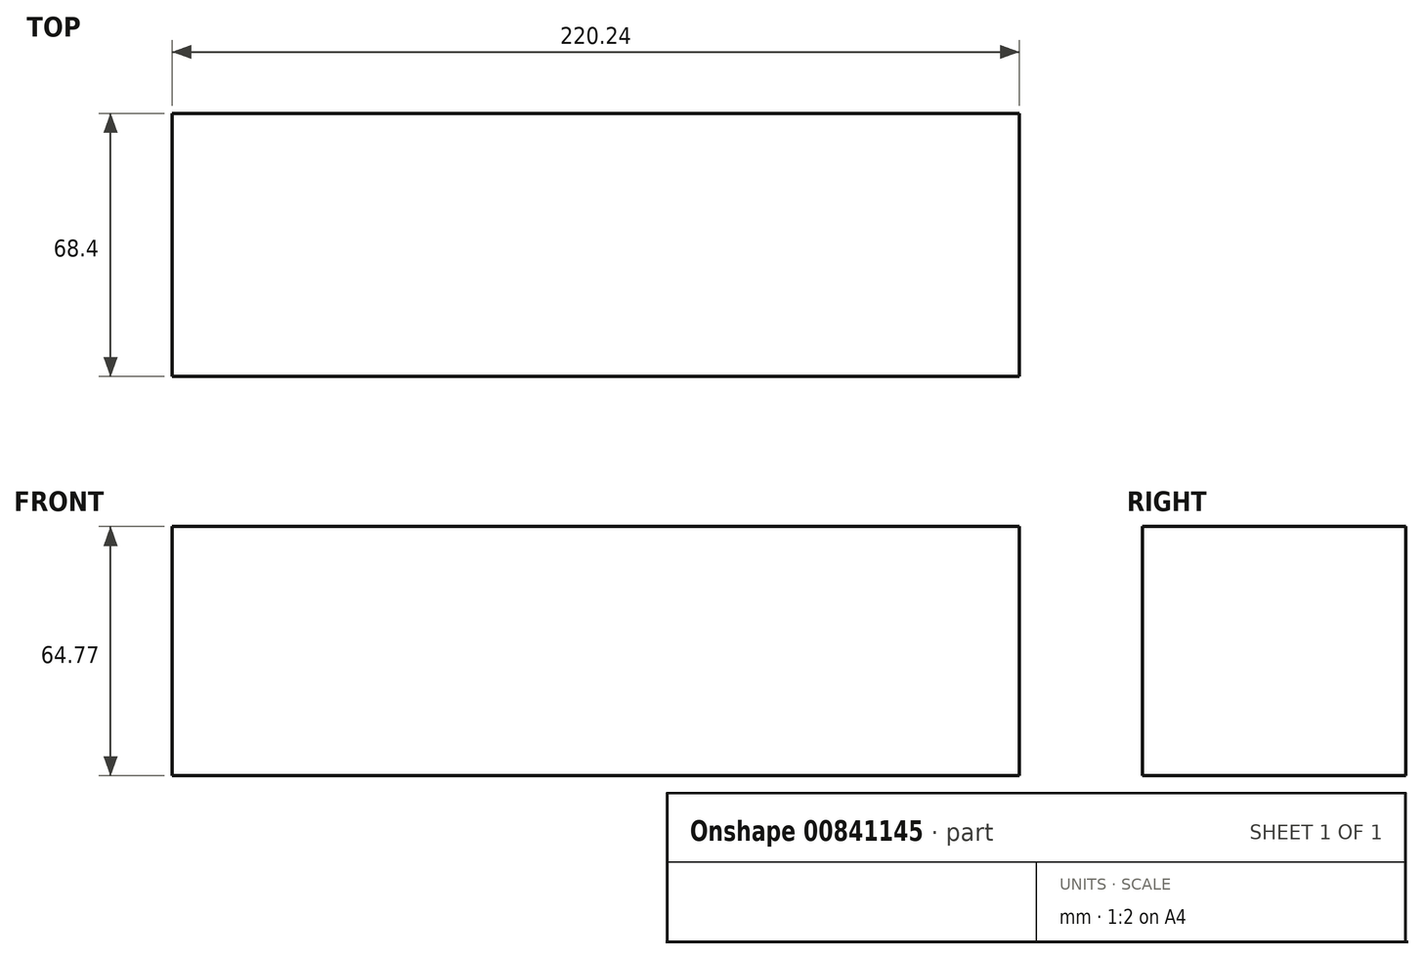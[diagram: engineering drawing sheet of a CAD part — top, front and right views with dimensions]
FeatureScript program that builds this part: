
annotation { "Feature Type Name" : "Feature", "Feature Type Description" : "" }
export const myFeature = defineFeature(function(context is Context, id is Id, definition is map)
    precondition{}
    {
        {
            var Q0;
            Q0=qCreatedBy(makeId("Top.planeOp"),FACE);
            var sketch = newSketch(context, id + "F0", { "sketchPlane" : qUnion([Q0])});
            skLineSegment(sketch, "E0.bottom", {"start": v(-44.21, -20.44) * mm, "end": v(34.67, -20.44) * mm});
            skLineSegment(sketch, "E0.top", {"start": v(-44.21, 47.96) * mm, "end": v(34.67, 47.96) * mm});
            skLineSegment(sketch, "E0.left", {"start": v(-44.21, -20.44) * mm, "end": v(-44.21, 47.96) * mm});
            skLineSegment(sketch, "E0.right", {"start": v(34.67, -20.44) * mm, "end": v(34.67, 47.96) * mm});
            skSolve(sketch);
        }
        {
            var Q0;
            Q0 = qSketchRegion(id + "F0", true);
            extrude(context, id + "F1", {"entities" : qUnion([Q0]), "depth" : 64.77 * mm, "offsetDistance" : 25.4 * mm});
        }
        {
            var Q0;
            Q0=makeQuery(id+"F1.opExtrude","SWEPT_FACE",FACE,{"disambiguationData":[OSD([sQuery(id+"F0.wireOp",EDGE,"E0.left")])]});
            extrude(context, id + "F2", {"entities" : qUnion([Q0]), "operationType" : NewBodyOperationType.ADD, "depth" : 141.36 * mm, "offsetDistance" : 25.4 * mm});
        }
    });
